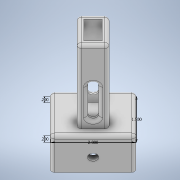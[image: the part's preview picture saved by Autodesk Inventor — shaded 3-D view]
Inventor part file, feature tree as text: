
AUTODESK INVENTOR PART (.ipt)
format: ipt  version: 2020 (Build 240168000, 168)  size: 215,040 bytes
history: native  units: in
note: dims shown in document units (in); Inventor stores cm internally (conversion verified against a paired STEP export)
features: extrude x4, sketch x3, hole x1, fillet x1
ambient origin geometry x8: Origin, YZ Plane, XZ Plane, XY Plane, X Axis, Y Axis, Z Axis, Center Point
bodies: Solid1 (feature_tree)
feature tree (9):
  sketch  "Sketch1"  dims[d0=1.5in d1=2.0in]
  extrude  "Extrusion1"  Depth=2.0in
  extrude  "Extrusion2"  Depth=0.2in
  hole  "Hole1"  [1 undecoded]
  extrude  "Extrusion3"  Depth=0.1in
  extrude  "Extrusion4"  Depth=1.0in
  fillet  "Fillet1"  Radius=0.7441in
  sketch  "Sketch2"  dims[d2=0.2in d3=0.2in]
  sketch  "Sketch4"  dims[d4=1.0in d5=0.0in d6=0.2in d7=0.0in d8=0.5in d9=0.266in d10=0.75in d11=0.438in d12=0.25in d13=0.5635in d14=1.0in d15=0.8108in d16=1.0in d17=0.7441in d18=1.0276in d19=0.4291in d20=0.7126in d21=2.75in d22=0.0in d23=0.372in d24=1.0in d25=0.25in d26=3.0in d27=0.0in d28=0.1in]
note: 1 required parameter value undecoded (feature->parameter linkage not recoverable at this tier; creation-order binding heuristic only, values carry confidence <= 0.55)
